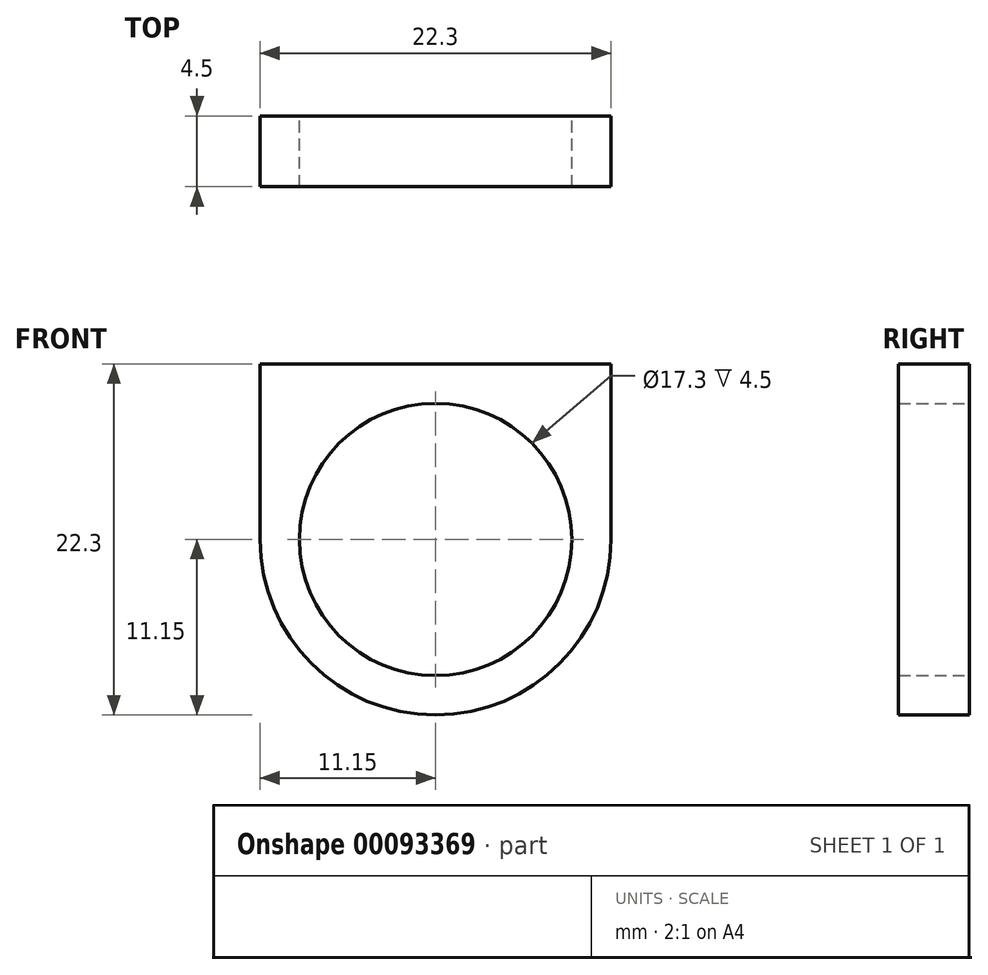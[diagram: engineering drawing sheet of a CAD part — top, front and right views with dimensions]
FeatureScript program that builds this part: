
annotation { "Feature Type Name" : "Feature", "Feature Type Description" : "" }
export const myFeature = defineFeature(function(context is Context, id is Id, definition is map)
    precondition{}
    {
        {
            var Q0;
            Q0=qCreatedBy(makeId("Front.planeOp"),FACE);
            var sketch = newSketch(context, id + "F0", { "sketchPlane" : qUnion([Q0])});
            skCircle(sketch, "E0", {"center": v(0, 0) * mm, "radius": 8.65 * mm});
            skCircle(sketch, "E1.0", {"center": v(0, 0) * mm, "radius": 11.15 * mm});
            skPoint(sketch, "E2", {"position": v(0, 11.15) * mm});
            skPoint(sketch, "E3", {"position": v(11.15, 0) * mm});
            skPoint(sketch, "E4", {"position": v(-11.15, 0) * mm});
            skLineSegment(sketch, "E5", {"start": v(11.15, 0) * mm, "end": v(11.15, 11.15) * mm});
            skLineSegment(sketch, "E6", {"start": v(11.15, 11.15) * mm, "end": v(0, 11.15) * mm});
            skLineSegment(sketch, "E7.MirrorCS", {"start": v(-11.15, 11.15) * mm, "end": v(0, 11.15) * mm});
            skLineSegment(sketch, "E8.MirrorCS", {"start": v(-11.15, 0) * mm, "end": v(-11.15, 11.15) * mm});
            skLineSegment(sketch, "E9", {"start": v(0, 11.15) * mm, "end": v(0, 13.15) * mm, "construction": true});
            skArc(sketch, "E10", {"start": v(0, 11.15) * mm, "mid": v(2, 13.15) * mm, "end": v(0, 15.15) * mm});
            skLineSegment(sketch, "E11", {"start": v(0, 15.15) * mm, "end": v(-11.15, 15.15) * mm});
            skLineSegment(sketch, "E12", {"start": v(-11.15, 15.15) * mm, "end": v(-11.15, 17.23) * mm});
            skLineSegment(sketch, "E13", {"start": v(-11.15, 17.23) * mm, "end": v(11.15, 17.23) * mm});
            skLineSegment(sketch, "E14", {"start": v(11.15, 17.23) * mm, "end": v(11.15, 15.15) * mm});
            skLineSegment(sketch, "E15", {"start": v(11.15, 15.15) * mm, "end": v(0, 15.15) * mm});
            skLineSegment(sketch, "E16", {"start": v(0, 13.15) * mm, "end": v(2, 13.15) * mm});
            skLineSegment(sketch, "E17.MirrorCS", {"start": v(0, 13.15) * mm, "end": v(-2, 13.15) * mm});
            skLineSegment(sketch, "E18", {"start": v(-11.15, 15.15) * mm, "end": v(-11.15, 11.15) * mm, "construction": true});
            skLineSegment(sketch, "E19", {"start": v(-11.15, 13.15) * mm, "end": v(-9.15, 13.15) * mm, "construction": true});
            skArc(sketch, "E20", {"start": v(-9.15, 15.15) * mm, "mid": v(-11.15, 13.15) * mm, "end": v(-9.15, 11.15) * mm});
            skPoint(sketch, "E21", {"position": v(-4, 15.15) * mm});
            skPoint(sketch, "E22", {"position": v(-4, 11.15) * mm});
            skPoint(sketch, "E23", {"position": v(-9.15, 15.15) * mm});
            skPoint(sketch, "E24", {"position": v(-9.15, 11.15) * mm});
            skLineSegment(sketch, "E25", {"start": v(0, 13.15) * mm, "end": v(-4, 13.15) * mm});
            skArc(sketch, "E26", {"start": v(-4, 15.15) * mm, "mid": v(-6, 13.15) * mm, "end": v(-4, 11.15) * mm});
            skSolve(sketch);
        }
        {
            var Q0;
            Q0=makeQuery(id+"F0.imprint","IMPRINT",FACE,{"disambiguationData":[TD([[makeQuery(id+"F0.imprint","IMPRINT",EDGE,{"derivedFrom":sQuery(id+"F0.wireOp",EDGE,"E0")}),-1.0]])]});
            var Q1;
            {var subQ0=sQuery(id+"F0.wireOp",EDGE,"E7.MirrorCS");Q1=makeQuery(id+"F0.imprint","IMPRINT",FACE,{"disambiguationData":[TD([[makeQuery(id+"F0.imprint","IMPRINT",EDGE,{"derivedFrom":subQ0}),-1.0]])]});}
            var Q2;
            {var subQ0=sQuery(id+"F0.wireOp",EDGE,"E5");Q2=makeQuery(id+"F0.imprint","IMPRINT",FACE,{"disambiguationData":[TD([[makeQuery(id+"F0.imprint","IMPRINT",EDGE,{"derivedFrom":subQ0}),1.0]])]});}
            extrude(context, id + "F1", {"entities" : qUnion([Q0, Q1, Q2]), "depth" : 2.25 * mm, "hasSecondDirection" : true, "secondDirectionOppositeDirection" : true, "secondDirectionDepth" : 2.25 * mm});
        }
        {
            var Q0;
            Q0=makeQuery(id+"F1.opExtrude","SWEPT_FACE",FACE,{"disambiguationData":[OSD([sQuery(id+"F0.wireOp",EDGE,"E6"),sQuery(id+"F0.wireOp",EDGE,"E7.MirrorCS")])]});
            cPlane(context, id + "F2", {"entities" : qUnion([Q0]), "cplaneType" : CPlaneType.OFFSET, "offset" : 2 * mm, "width" : 150 * mm, "height" : 150 * mm});
        }
        {
            var Q0;
            Q0=qCreatedBy(id+"F2.planeOp",FACE);
            var sketch = newSketch(context, id + "F3", { "sketchPlane" : qUnion([Q0])});
            skLineSegment(sketch, "E27", {"start": v(0, 0) * mm, "end": v(-4, 0) * mm, "construction": true});
            skLineSegment(sketch, "E28", {"start": v(0, 0) * mm, "end": v(-9.15, 0) * mm, "construction": true});
            skCircle(sketch, "E29", {"center": v(-4, 0) * mm, "radius": 2 * mm});
            skCircle(sketch, "E30", {"center": v(-9.15, 0) * mm, "radius": 2 * mm});
            skSolve(sketch);
        }
        {
            var Q0;
            Q0=sQuery(id+"F0.wireOp",EDGE,"E20");
            var Q1;
            Q1=sQuery(id+"F3.wireOp",EDGE,"E30");
            revolve(context, id + "F4", {"bodyType" : ToolBodyType.SURFACE, "surfaceEntities" : qUnion([Q0]), "axis" : qUnion([Q1]), "revolveType" : RevolveType.FULL});
        }
    });
